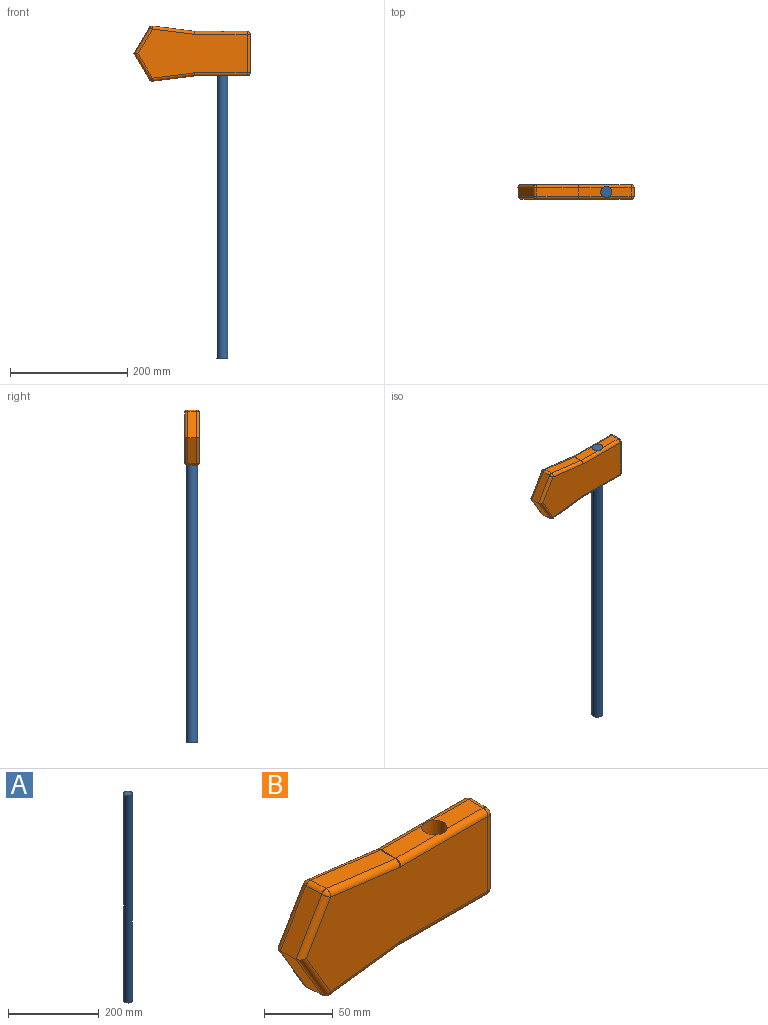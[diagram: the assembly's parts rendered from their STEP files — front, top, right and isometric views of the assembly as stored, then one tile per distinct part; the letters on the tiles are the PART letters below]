
ASSEMBLY  parts=2 mates=1
PART A: 3 faces, bbox 19.1x19.1x558 mm
  f0: cylinder r=9.54mm len=557.98mm, axis (0,0,1), area 33461.4mm2, adj f1,f2
  f1: plane 19.09x19.09mm, normal (0,0,1), area 286.2mm2, adj f0
  f2: plane 19.09x19.09mm, normal (0,0,-1), area 286.2mm2, adj f0
PART B: 44 faces, bbox 198.3x25.4x94.3 mm
  f0: plane 37.15x15.24mm, normal (0,0,1), area 522.9mm2, adj f11,f19,f26,f27
  f1: plane 41.91x15.24mm, normal (0,0,-1), area 595.4mm2, adj f11,f29,f39,f43
  f2: plane 41.91x15.24mm, normal (0,0,1), area 595.4mm2, adj f11,f18,f19,f26
  f3: plane 71.69x15.24mm, normal (0.12,0,0.99), area 1094.5mm2, adj f12,f16,f17,f18
  f4: plane 44.68x27.36mm, normal (-0.86,-0.05,0.51), area 791.7mm2, adj f5,f15,f16,f25
  f5: plane 44.68x27.36mm, normal (-0.86,-0.05,-0.51), area 791.7mm2, adj f4,f20,f31,f32
  f6: plane 71.69x15.24mm, normal (0.12,0,-0.99), area 1094.5mm2, adj f30,f31,f39,f40
  f7: plane 37.15x15.24mm, normal (0,0,-1), area 522.9mm2, adj f11,f29,f38,f43
  f8: plane 66.04x15.24mm, normal (1,0,0), area 1006.4mm2, adj f27,f28,f37,f38
  f9: plane 186.38x83.96mm, normal (0,-1,0), area 12349.9mm2, adj f17,f22,f25,f26,f32,f37,f40,f42
  f10: plane 187.31x84.17mm, normal (0,1,0), area 12427.9mm2, adj f12,f14,f15,f19,f20,f28,f29,f30
  f11: cylinder r=9.21mm len=76.2mm, axis (0,0,1), area 4402.5mm2, adj f0,f1,f2,f7,f19,f26,f29,f43
  f12: cylinder r=5.08mm len=72.33mm, axis (-0.99,0,0.12), area 576.6mm2, adj f3,f10,f13,f14
  f13: sphere r=5.08mm, area 30.8mm2, adj f12,f15,f16
  f14: torus R=10.16mm, axis (0,-1,0), area 6.9mm2, adj f10,f12,f18,f19
  f15: cylinder r=5.08mm len=47.27mm, axis (0.51,0,0.86), area 419.6mm2, adj f4,f10,f13,f20
  f16: cylinder r=5.08mm len=15.51mm, axis (0.06,-1,-0.01), area 90mm2, adj f3,f4,f13,f21
  f17: cylinder r=5.08mm len=71.46mm, axis (0.99,0,-0.12), area 569.6mm2, adj f3,f9,f21,f22
  f18: cylinder r=5.08mm len=15.24mm, axis (0,1,0), area 9.7mm2, adj f2,f3,f14,f22
  f19: cylinder r=5.08mm len=89.39mm, axis (-1,0,0), area 702mm2, adj f0,f2,f10,f11,f14,f23
  f20: cylinder r=5.08mm len=47.27mm, axis (-0.51,0,0.86), area 419.6mm2, adj f5,f10,f15,f24
  f21: sphere r=5.08mm, area 29mm2, adj f16,f17,f25
  f22: torus R=10.16mm, axis (0,-1,0), area 6.9mm2, adj f9,f17,f18,f26
  f23: sphere r=5.08mm, area 40.5mm2, adj f19,f27,f28
  f24: sphere r=5.08mm, area 30.8mm2, adj f20,f30,f31
  f25: cylinder r=5.08mm len=47.15mm, axis (-0.51,0,-0.86), area 391mm2, adj f4,f9,f21,f32
  f26: cylinder r=5.08mm len=89.39mm, axis (1,0,0), area 702mm2, adj f0,f2,f9,f11,f22,f33
  f27: cylinder r=5.08mm len=15.24mm, axis (0,1,0), area 121.6mm2, adj f0,f8,f23,f33
  f28: cylinder r=5.08mm len=66.04mm, axis (0,0,1), area 527mm2, adj f8,f10,f23,f34
  f29: cylinder r=5.08mm len=89.39mm, axis (1,0,0), area 702mm2, adj f1,f7,f10,f11,f34,f35
  f30: cylinder r=5.08mm len=72.33mm, axis (0.99,0,0.12), area 576.6mm2, adj f6,f10,f24,f35
  f31: cylinder r=5.08mm len=15.51mm, axis (-0.06,1,-0.01), area 90mm2, adj f5,f6,f24,f36
  f32: cylinder r=5.08mm len=47.15mm, axis (0.51,0,-0.86), area 391mm2, adj f5,f9,f25,f36
  f33: sphere r=5.08mm, area 40.5mm2, adj f26,f27,f37
  f34: sphere r=5.08mm, area 40.5mm2, adj f28,f29,f38
  f35: torus R=10.16mm, axis (0,-1,0), area 6.9mm2, adj f10,f29,f30,f39
  f36: sphere r=5.08mm, area 29mm2, adj f31,f32,f40
  f37: cylinder r=5.08mm len=66.04mm, axis (0,0,-1), area 527mm2, adj f8,f9,f33,f41
  f38: cylinder r=5.08mm len=15.24mm, axis (0,1,0), area 121.6mm2, adj f7,f8,f34,f41
  f39: cylinder r=5.08mm len=15.24mm, axis (0,-1,0), area 9.7mm2, adj f1,f6,f35,f42
  f40: cylinder r=5.08mm len=71.46mm, axis (-0.99,0,-0.12), area 569.6mm2, adj f6,f9,f36,f42
  f41: sphere r=5.08mm, area 40.5mm2, adj f37,f38,f43
  f42: torus R=10.16mm, axis (0,-1,0), area 6.9mm2, adj f9,f39,f40,f43
  f43: cylinder r=5.08mm len=89.39mm, axis (-1,0,0), area 702mm2, adj f1,f7,f9,f11,f41,f42
PLACE A t=(47.47,94.97,-171.11)mm
PLACE B t=(21.58,107.67,-133.16)mm
MATE fastened B.f11 <-> A.f0  axis (0,0,1) through (-14.4,94.97,-92.39)mm
